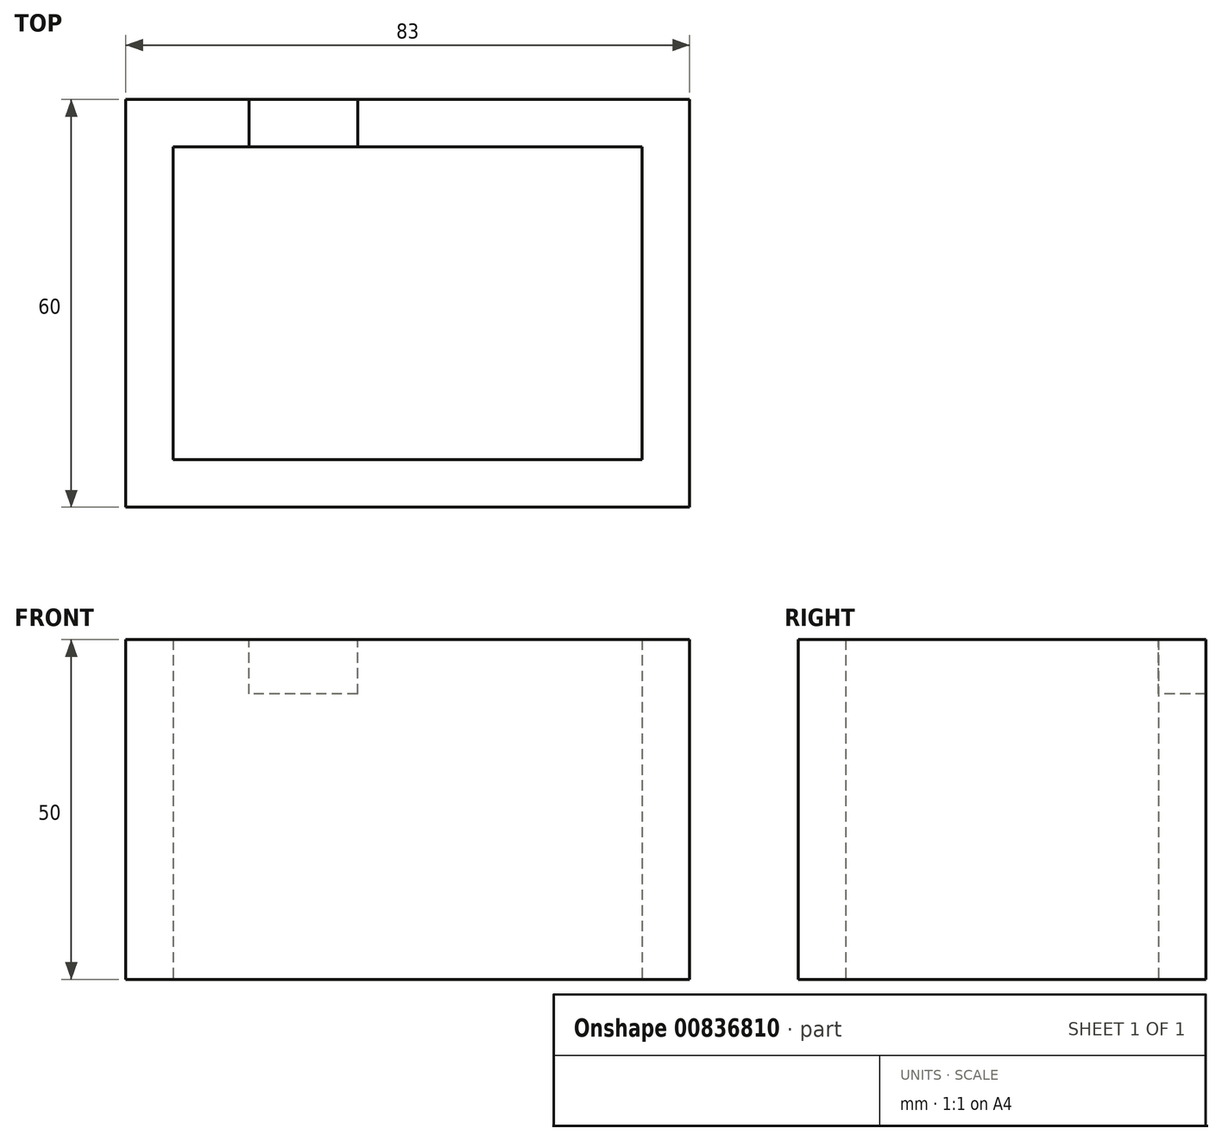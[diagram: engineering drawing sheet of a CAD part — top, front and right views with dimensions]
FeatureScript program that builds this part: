
annotation { "Feature Type Name" : "Feature", "Feature Type Description" : "" }
export const myFeature = defineFeature(function(context is Context, id is Id, definition is map)
    precondition{}
    {
        {
            var Q0;
            Q0=qCreatedBy(makeId("Top.planeOp"),FACE);
            var sketch = newSketch(context, id + "F0", { "sketchPlane" : qUnion([Q0])});
            skLineSegment(sketch, "E0.bottom", {"start": v(41.5, -30) * mm, "end": v(-41.5, -30) * mm});
            skLineSegment(sketch, "E0.top", {"start": v(41.5, 30) * mm, "end": v(-41.5, 30) * mm});
            skLineSegment(sketch, "E0.left", {"start": v(41.5, -30) * mm, "end": v(41.5, 30) * mm});
            skLineSegment(sketch, "E0.right", {"start": v(-41.5, -30) * mm, "end": v(-41.5, 30) * mm});
            skPoint(sketch, "E0.middle", {"position": v(0, 0) * mm});
            skLineSegment(sketch, "E1.bottom", {"start": v(34.5, -23) * mm, "end": v(-34.5, -23) * mm});
            skLineSegment(sketch, "E1.top", {"start": v(34.5, 23) * mm, "end": v(-34.5, 23) * mm});
            skLineSegment(sketch, "E1.left", {"start": v(34.5, -23) * mm, "end": v(34.5, 23) * mm});
            skLineSegment(sketch, "E1.right", {"start": v(-34.5, -23) * mm, "end": v(-34.5, 23) * mm});
            skSolve(sketch);
        }
        {
            var Q0;
            Q0=makeQuery(id+"F0.imprint","IMPRINT",FACE,{"disambiguationData":[TD([[makeQuery(id+"F0.imprint","IMPRINT",EDGE,{"derivedFrom":sQuery(id+"F0.wireOp",EDGE,"E0.bottom")}),-1.0]])]});
            extrude(context, id + "F1", {"entities" : qUnion([Q0]), "depth" : 50 * mm, "offsetDistance" : 25 * mm});
        }
        {
            var Q0;
            Q0=makeQuery(id+"F1.opExtrude","CAP_FACE",FACE,{"disambiguationData":[OSD([sQuery(id+"F0.wireOp",EDGE,"E0.bottom"),sQuery(id+"F0.wireOp",EDGE,"E0.top"),sQuery(id+"F0.wireOp",EDGE,"E0.left"),sQuery(id+"F0.wireOp",EDGE,"E0.right"),sQuery(id+"F0.wireOp",EDGE,"E1.bottom"),sQuery(id+"F0.wireOp",EDGE,"E1.top"),sQuery(id+"F0.wireOp",EDGE,"E1.left"),sQuery(id+"F0.wireOp",EDGE,"E1.right")])],"isStart":false});
            var sketch = newSketch(context, id + "F2", { "sketchPlane" : qUnion([Q0])});
            skLineSegment(sketch, "E2.bottom", {"start": v(-23.37, 30) * mm, "end": v(-7.37, 30) * mm});
            skLineSegment(sketch, "E2.top", {"start": v(-23.37, 23) * mm, "end": v(-7.37, 23) * mm});
            skLineSegment(sketch, "E2.left", {"start": v(-23.37, 30) * mm, "end": v(-23.37, 23) * mm});
            skLineSegment(sketch, "E2.right", {"start": v(-7.37, 30) * mm, "end": v(-7.37, 23) * mm});
            skSolve(sketch);
        }
        {
            var Q0;
            Q0 = qSketchRegion(id + "F2", true);
            extrude(context, id + "F3", {"entities" : qUnion([Q0]), "operationType" : NewBodyOperationType.REMOVE, "oppositeDirection" : true, "depth" : 8 * mm, "offsetDistance" : 25 * mm});
        }
    });
